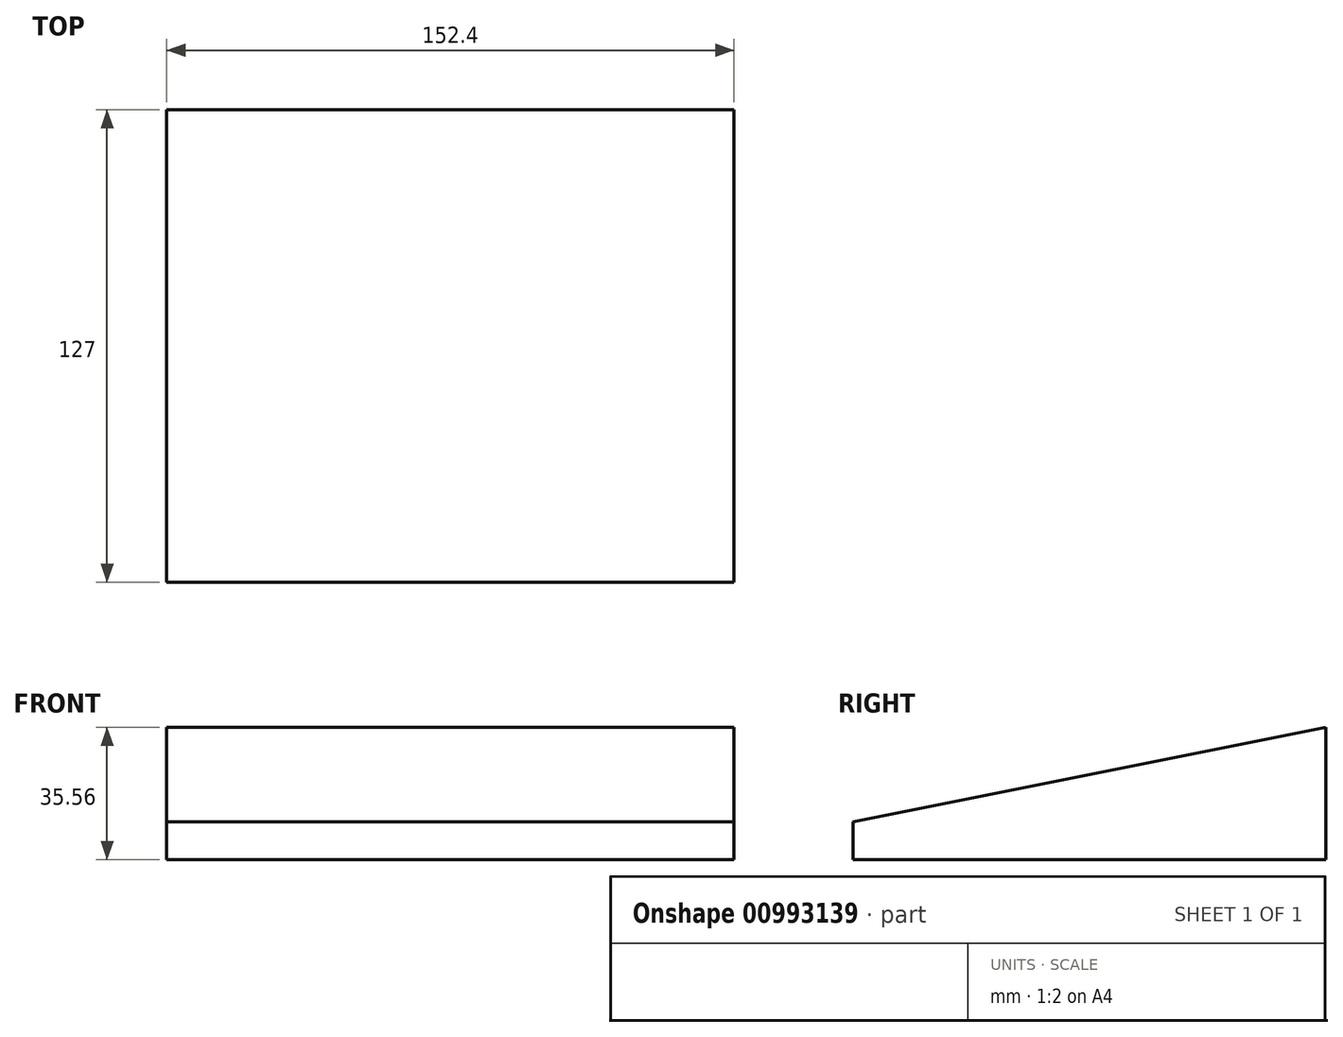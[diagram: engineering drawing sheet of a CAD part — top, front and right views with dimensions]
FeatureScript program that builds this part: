
annotation { "Feature Type Name" : "Feature", "Feature Type Description" : "" }
export const myFeature = defineFeature(function(context is Context, id is Id, definition is map)
    precondition{}
    {
        {
            var Q0;
            Q0=qCreatedBy(makeId("Right.planeOp"),FACE);
            var sketch = newSketch(context, id + "F0", { "sketchPlane" : qUnion([Q0])});
            skLineSegment(sketch, "E0.bottom", {"start": v(-80.3, 59.1) * mm, "end": v(46.7, 59.1) * mm});
            skLineSegment(sketch, "E0.top", {"start": v(-80.3, 23.53) * mm, "end": v(46.7, 23.53) * mm});
            skLineSegment(sketch, "E0.left", {"start": v(-80.3, 59.1) * mm, "end": v(-80.3, 23.53) * mm});
            skLineSegment(sketch, "E0.right", {"start": v(46.7, 59.1) * mm, "end": v(46.7, 23.53) * mm});
            skLineSegment(sketch, "E1", {"start": v(-80.3, 33.7) * mm, "end": v(46.7, 59.1) * mm});
            skSolve(sketch);
        }
        {
            var Q0;
            {var subQ0=sQuery(id+"F0.wireOp",EDGE,"E0.top");Q0=makeQuery(id+"F0.imprint","IMPRINT",FACE,{"disambiguationData":[TD([[makeQuery(id+"F0.imprint","IMPRINT",EDGE,{"derivedFrom":subQ0}),1.0]])]});}
            extrude(context, id + "F1", {"entities" : qUnion([Q0]), "depth" : 152.4 * mm, "offsetDistance" : 25.4 * mm});
        }
    });
